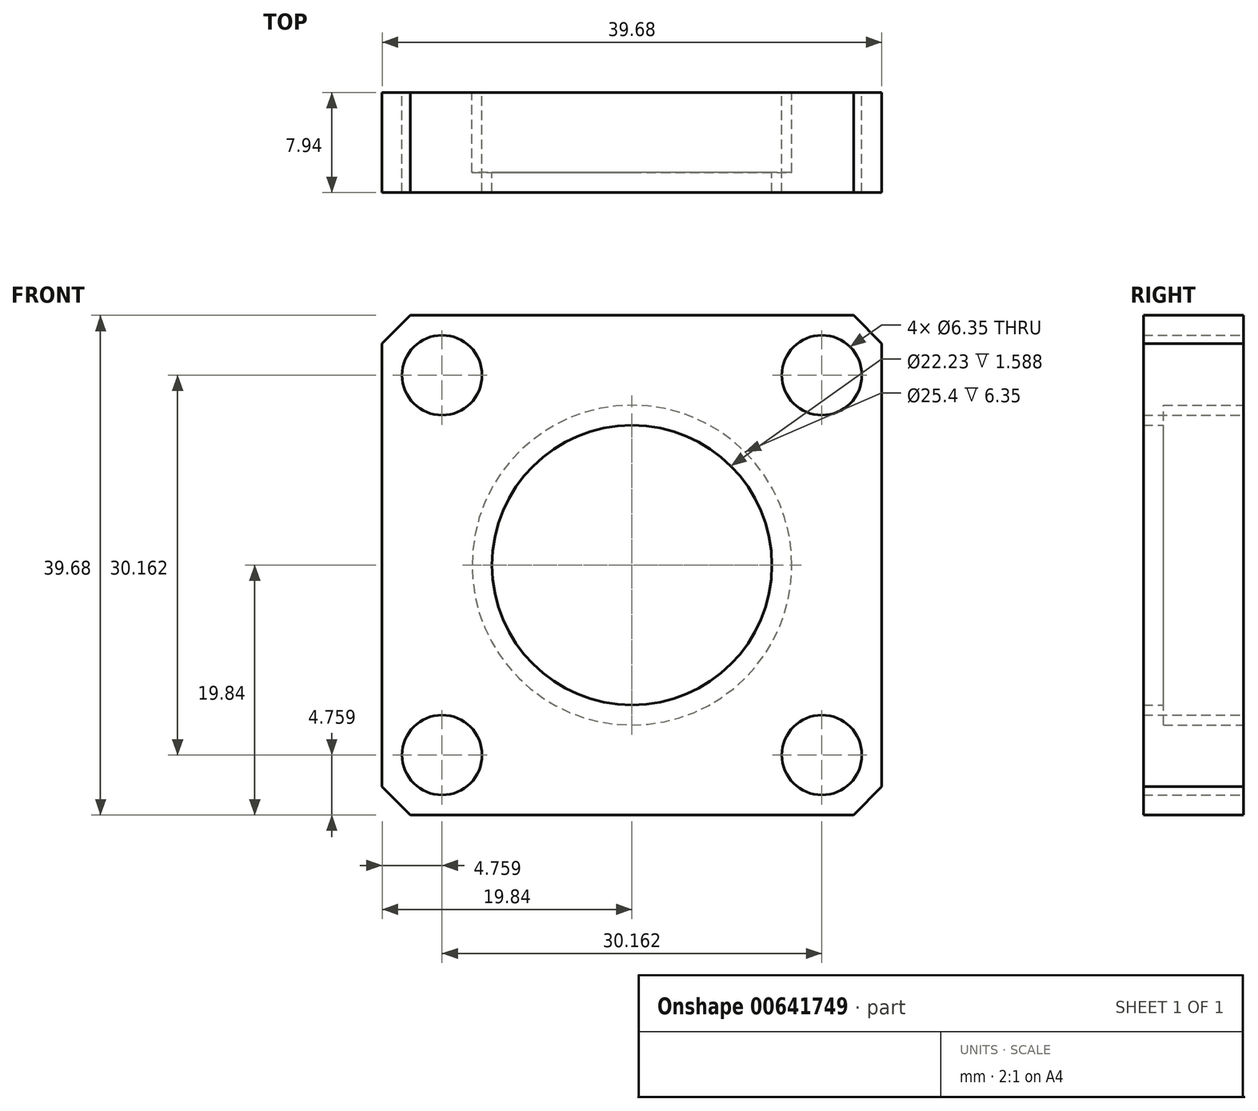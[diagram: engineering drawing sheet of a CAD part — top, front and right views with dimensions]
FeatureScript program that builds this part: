
annotation { "Feature Type Name" : "Feature", "Feature Type Description" : "" }
export const myFeature = defineFeature(function(context is Context, id is Id, definition is map)
    precondition{}
    {
        {
            var Q0;
            Q0=qCreatedBy(makeId("Front.planeOp"),FACE);
            var sketch = newSketch(context, id + "F0", { "sketchPlane" : qUnion([Q0])});
            skLineSegment(sketch, "E0.bottom", {"start": v(19.84, -19.84) * mm, "end": v(-19.84, -19.84) * mm});
            skLineSegment(sketch, "E0.top", {"start": v(19.84, 19.84) * mm, "end": v(-19.84, 19.84) * mm});
            skLineSegment(sketch, "E0.left", {"start": v(19.84, -19.84) * mm, "end": v(19.84, 19.84) * mm});
            skLineSegment(sketch, "E0.right", {"start": v(-19.84, -19.84) * mm, "end": v(-19.84, 19.84) * mm});
            skPoint(sketch, "E0.middle", {"position": v(0, 0) * mm});
            skCircle(sketch, "E1", {"center": v(0, 0) * mm, "radius": 12.7 * mm});
            skCircle(sketch, "E2", {"center": v(0, 0) * mm, "radius": 11.11 * mm});
            skCircle(sketch, "E3", {"center": v(-15.08, 15.08) * mm, "radius": 3.18 * mm});
            skCircle(sketch, "E4.MirrorC", {"center": v(15.08, 15.08) * mm, "radius": 3.18 * mm});
            skCircle(sketch, "E5.MirrorC", {"center": v(-15.08, -15.08) * mm, "radius": 3.18 * mm});
            skCircle(sketch, "E6.MirrorC", {"center": v(15.08, -15.08) * mm, "radius": 3.18 * mm});
            skSolve(sketch);
        }
        {
            var Q0;
            Q0=makeQuery(id+"F0.imprint","IMPRINT",FACE,{"disambiguationData":[TD([[makeQuery(id+"F0.imprint","IMPRINT",EDGE,{"derivedFrom":sQuery(id+"F0.wireOp",EDGE,"E0.bottom")}),-1.0]])]});
            var Q1;
            Q1=makeQuery(id+"F0.imprint","IMPRINT",FACE,{"disambiguationData":[TD([[makeQuery(id+"F0.imprint","IMPRINT",EDGE,{"derivedFrom":sQuery(id+"F0.wireOp",EDGE,"E1")}),1.0]])]});
            extrude(context, id + "F1", {"entities" : qUnion([Q0, Q1]), "depth" : 7.94 * mm, "offsetDistance" : 25.4 * mm});
        }
        {
            var Q0;
            Q0=makeQuery(id+"F0.imprint","IMPRINT",FACE,{"disambiguationData":[TD([[makeQuery(id+"F0.imprint","IMPRINT",EDGE,{"derivedFrom":sQuery(id+"F0.wireOp",EDGE,"E1")}),1.0]])]});
            extrude(context, id + "F2", {"entities" : qUnion([Q0]), "operationType" : NewBodyOperationType.REMOVE, "depth" : 6.35 * mm, "offsetDistance" : 25.4 * mm});
        }
        {
            var Q0;
            Q0=makeQuery(id+"F1.opExtrude","SWEPT_EDGE",EDGE,{"disambiguationData":[OSD([sQuery(id+"F0.wireOp",EDGE,"E0.top"),sQuery(id+"F0.wireOp",EDGE,"E0.left")])]});
            var Q1;
            Q1=makeQuery(id+"F1.opExtrude","SWEPT_EDGE",EDGE,{"disambiguationData":[OSD([sQuery(id+"F0.wireOp",EDGE,"E0.bottom"),sQuery(id+"F0.wireOp",EDGE,"E0.left")])]});
            var Q2;
            Q2=makeQuery(id+"F1.opExtrude","SWEPT_EDGE",EDGE,{"disambiguationData":[OSD([sQuery(id+"F0.wireOp",EDGE,"E0.bottom"),sQuery(id+"F0.wireOp",EDGE,"E0.right")])]});
            var Q3;
            Q3=makeQuery(id+"F1.opExtrude","SWEPT_EDGE",EDGE,{"disambiguationData":[OSD([sQuery(id+"F0.wireOp",EDGE,"E0.top"),sQuery(id+"F0.wireOp",EDGE,"E0.right")])]});
            chamfer(context, id + "F3", {"entities" : qUnion([Q0, Q1, Q2, Q3]), "width" : 2.25 * mm, "tangentPropagation" : true});
        }
    });
